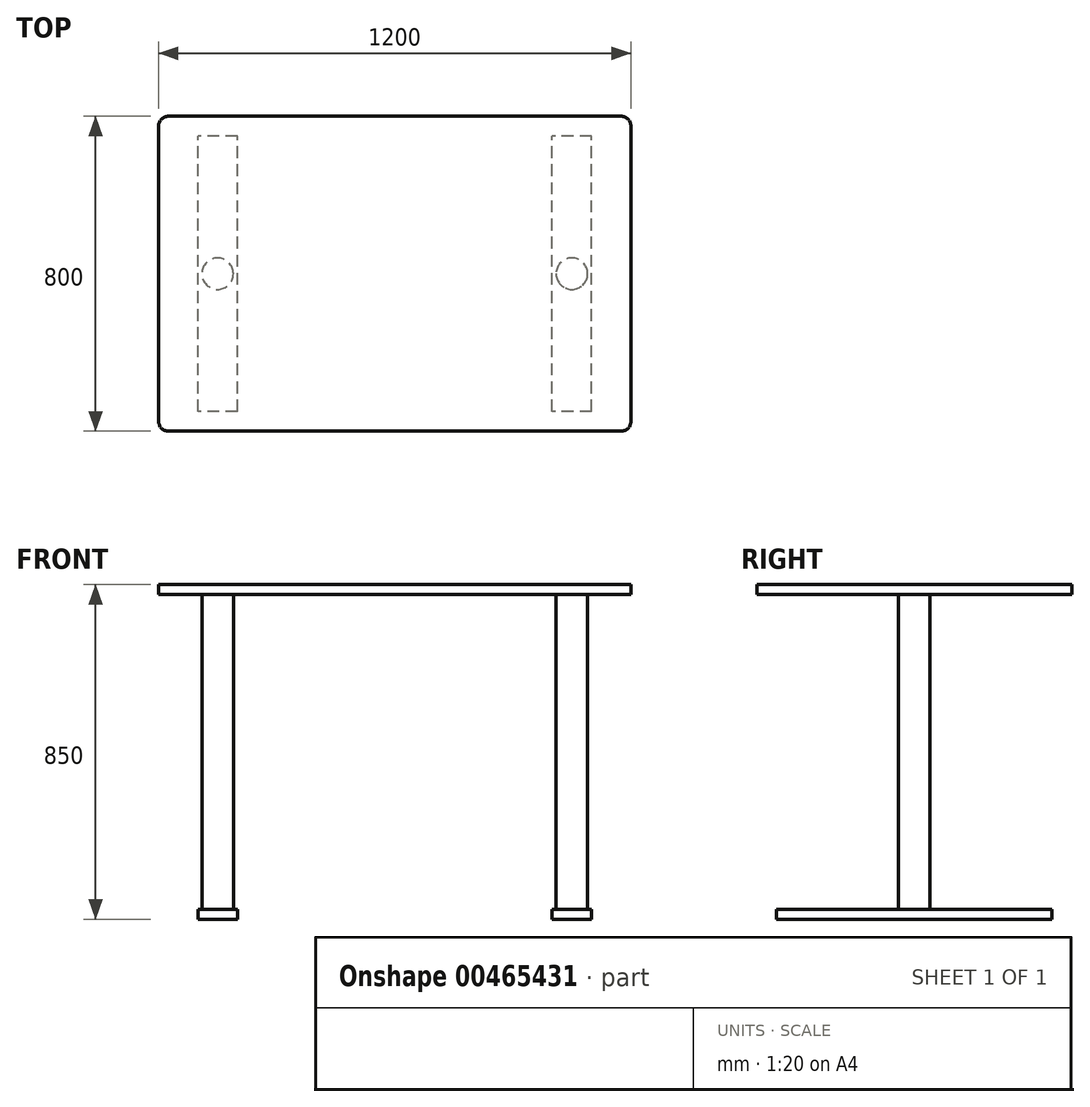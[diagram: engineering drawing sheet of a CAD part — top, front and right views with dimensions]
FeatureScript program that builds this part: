
annotation { "Feature Type Name" : "Feature", "Feature Type Description" : "" }
export const myFeature = defineFeature(function(context is Context, id is Id, definition is map)
    precondition{}
    {
        {
            var Q0;
            Q0=qCreatedBy(makeId("Top.planeOp"),FACE);
            var sketch = newSketch(context, id + "F0", { "sketchPlane" : qUnion([Q0])});
            skLineSegment(sketch, "E0.bottom", {"start": v(0, 0) * mm, "end": v(1200, 0) * mm});
            skLineSegment(sketch, "E0.top", {"start": v(0, 800) * mm, "end": v(1200, 800) * mm});
            skLineSegment(sketch, "E0.left", {"start": v(0, 0) * mm, "end": v(0, 800) * mm});
            skLineSegment(sketch, "E0.right", {"start": v(1200, 0) * mm, "end": v(1200, 800) * mm});
            skSolve(sketch);
        }
        {
            var Q0;
            Q0 = qSketchRegion(id + "F0", true);
            extrude(context, id + "F1", {"entities" : qUnion([Q0]), "depth" : 25 * mm});
        }
        {
            var Q0;
            Q0=makeQuery(id+"F1.opExtrude","CAP_FACE",FACE,{"disambiguationData":[OSD([sQuery(id+"F0.wireOp",EDGE,"E0.bottom"),sQuery(id+"F0.wireOp",EDGE,"E0.top"),sQuery(id+"F0.wireOp",EDGE,"E0.left"),sQuery(id+"F0.wireOp",EDGE,"E0.right")])],"isStart":true});
            var sketch = newSketch(context, id + "F2", { "sketchPlane" : qUnion([Q0])});
            skCircle(sketch, "E1", {"center": v(150, -400) * mm, "radius": 40 * mm});
            skPoint(sketch, "E1.centerSnap0", {"position": v(0, -400) * mm});
            skCircle(sketch, "E2", {"center": v(1050, -400) * mm, "radius": 40 * mm});
            skPoint(sketch, "E2.centerSnap0", {"position": v(1200, -400) * mm});
            skSolve(sketch);
        }
        {
            var Q0;
            Q0 = qSketchRegion(id + "F2", true);
            extrude(context, id + "F3", {"entities" : qUnion([Q0]), "operationType" : NewBodyOperationType.ADD, "depth" : 800 * mm});
        }
        {
            var Q0;
            Q0=makeQuery(id+"F3.opExtrude","CAP_FACE",FACE,{"disambiguationData":[OSD([sQuery(id+"F2.wireOp",EDGE,"E1")])],"isStart":false});
            var sketch = newSketch(context, id + "F4", { "sketchPlane" : qUnion([Q0])});
            skLineSegment(sketch, "E3.bottom", {"start": v(200, -50) * mm, "end": v(100, -50) * mm});
            skLineSegment(sketch, "E3.top", {"start": v(200, -750) * mm, "end": v(100, -750) * mm});
            skLineSegment(sketch, "E3.left", {"start": v(200, -50) * mm, "end": v(200, -750) * mm});
            skLineSegment(sketch, "E3.right", {"start": v(100, -50) * mm, "end": v(100, -750) * mm});
            skPoint(sketch, "E3.middle", {"position": v(150, -400) * mm});
            skSolve(sketch);
        }
        {
            var Q0;
            Q0 = qSketchRegion(id + "F4", true);
            extrude(context, id + "F5", {"entities" : qUnion([Q0]), "operationType" : NewBodyOperationType.ADD, "depth" : 25 * mm});
        }
        {
            var Q0;
            Q0=makeQuery(id+"F3.opExtrude","CAP_FACE",FACE,{"disambiguationData":[OSD([sQuery(id+"F2.wireOp",EDGE,"E2")])],"isStart":false});
            var sketch = newSketch(context, id + "F6", { "sketchPlane" : qUnion([Q0])});
            skLineSegment(sketch, "E4.bottom", {"start": v(1100, -50) * mm, "end": v(1000, -50) * mm});
            skLineSegment(sketch, "E4.top", {"start": v(1100, -750) * mm, "end": v(1000, -750) * mm});
            skLineSegment(sketch, "E4.left", {"start": v(1100, -50) * mm, "end": v(1100, -750) * mm});
            skLineSegment(sketch, "E4.right", {"start": v(1000, -50) * mm, "end": v(1000, -750) * mm});
            skPoint(sketch, "E4.middle", {"position": v(1050, -400) * mm});
            skSolve(sketch);
        }
        {
            var Q0;
            Q0 = qSketchRegion(id + "F6", true);
            extrude(context, id + "F7", {"entities" : qUnion([Q0]), "operationType" : NewBodyOperationType.ADD, "depth" : 25 * mm});
        }
        {
            var Q0;
            Q0=makeQuery(id+"F1.opExtrude","SWEPT_EDGE",EDGE,{"disambiguationData":[OSD([sQuery(id+"F0.wireOp",EDGE,"E0.bottom"),sQuery(id+"F0.wireOp",EDGE,"E0.right")])]});
            var Q1;
            Q1=makeQuery(id+"F1.opExtrude","SWEPT_EDGE",EDGE,{"disambiguationData":[OSD([sQuery(id+"F0.wireOp",EDGE,"E0.top"),sQuery(id+"F0.wireOp",EDGE,"E0.right")])]});
            var Q2;
            Q2=makeQuery(id+"F1.opExtrude","SWEPT_EDGE",EDGE,{"disambiguationData":[OSD([sQuery(id+"F0.wireOp",EDGE,"E0.bottom"),sQuery(id+"F0.wireOp",EDGE,"E0.left")])]});
            var Q3;
            Q3=makeQuery(id+"F1.opExtrude","SWEPT_EDGE",EDGE,{"disambiguationData":[OSD([sQuery(id+"F0.wireOp",EDGE,"E0.top"),sQuery(id+"F0.wireOp",EDGE,"E0.left")])]});
            fillet(context, id + "F8", {"entities" : qUnion([Q0, Q1, Q2, Q3]), "radius" : 25 * mm, "tangentPropagation" : true, "allowEdgeOverflow" : false});
        }
        {
            var Q0;
            Q0=makeQuery(id+"F1.opExtrude","SWEPT_BODY",BODY,{"disambiguationData":[OSD([sQuery(id+"F0.wireOp",EDGE,"E0.bottom"),sQuery(id+"F0.wireOp",EDGE,"E0.top"),sQuery(id+"F0.wireOp",EDGE,"E0.left"),sQuery(id+"F0.wireOp",EDGE,"E0.right")])]});
            transform(context, id + "F9", {"entities" : qUnion([Q0]), "transformType" : TransformType.TRANSLATION_3D, "dx" : 0 * mm, "dy" : 0 * mm, "dz" : 0 * mm, "makeCopy" : true});
        }
        {
            var Q0;
            Q0=makeQuery(id+"F9.opPattern","COPY",BODY,{"derivedFrom":makeQuery(id+"F1.opExtrude","SWEPT_BODY",BODY,{"disambiguationData":[OSD([sQuery(id+"F0.wireOp",EDGE,"E0.bottom"),sQuery(id+"F0.wireOp",EDGE,"E0.top"),sQuery(id+"F0.wireOp",EDGE,"E0.left"),sQuery(id+"F0.wireOp",EDGE,"E0.right")])]}),"instanceName":"1"});
            deleteBodies(context, id + "F10", {"entities" : qUnion([Q0])});
        }
    });
